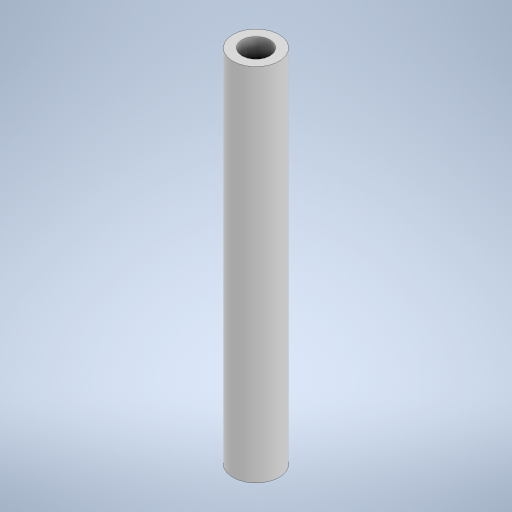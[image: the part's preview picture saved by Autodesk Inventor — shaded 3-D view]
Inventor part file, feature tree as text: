
AUTODESK INVENTOR PART (.ipt)
format: ipt  version: 2023 (Build 270158000, 158)  size: 235,008 bytes
history: native  units: in
note: dims shown in document units (in); Inventor stores cm internally (conversion verified against a paired STEP export)
features: extrude x2, sketch x1, mirror x1
ambient origin geometry x8: Origin, YZ Plane, XZ Plane, XY Plane, X Axis, Y Axis, Z Axis, Center Point
bodies: Solid1 (feature_tree)
feature tree (4):
  sketch  "Sketch1"  dims[d0=0.0938in d1=0.0563in d2=0.365in d3=0.0in d4=0.25in d5=0.0in]
  extrude  "Extrusion1"  Depth=0.25in
  extrude  "Extrusion2"  Depth=0.25in TaperAngle=0.0deg
  mirror  "Mirror1"
